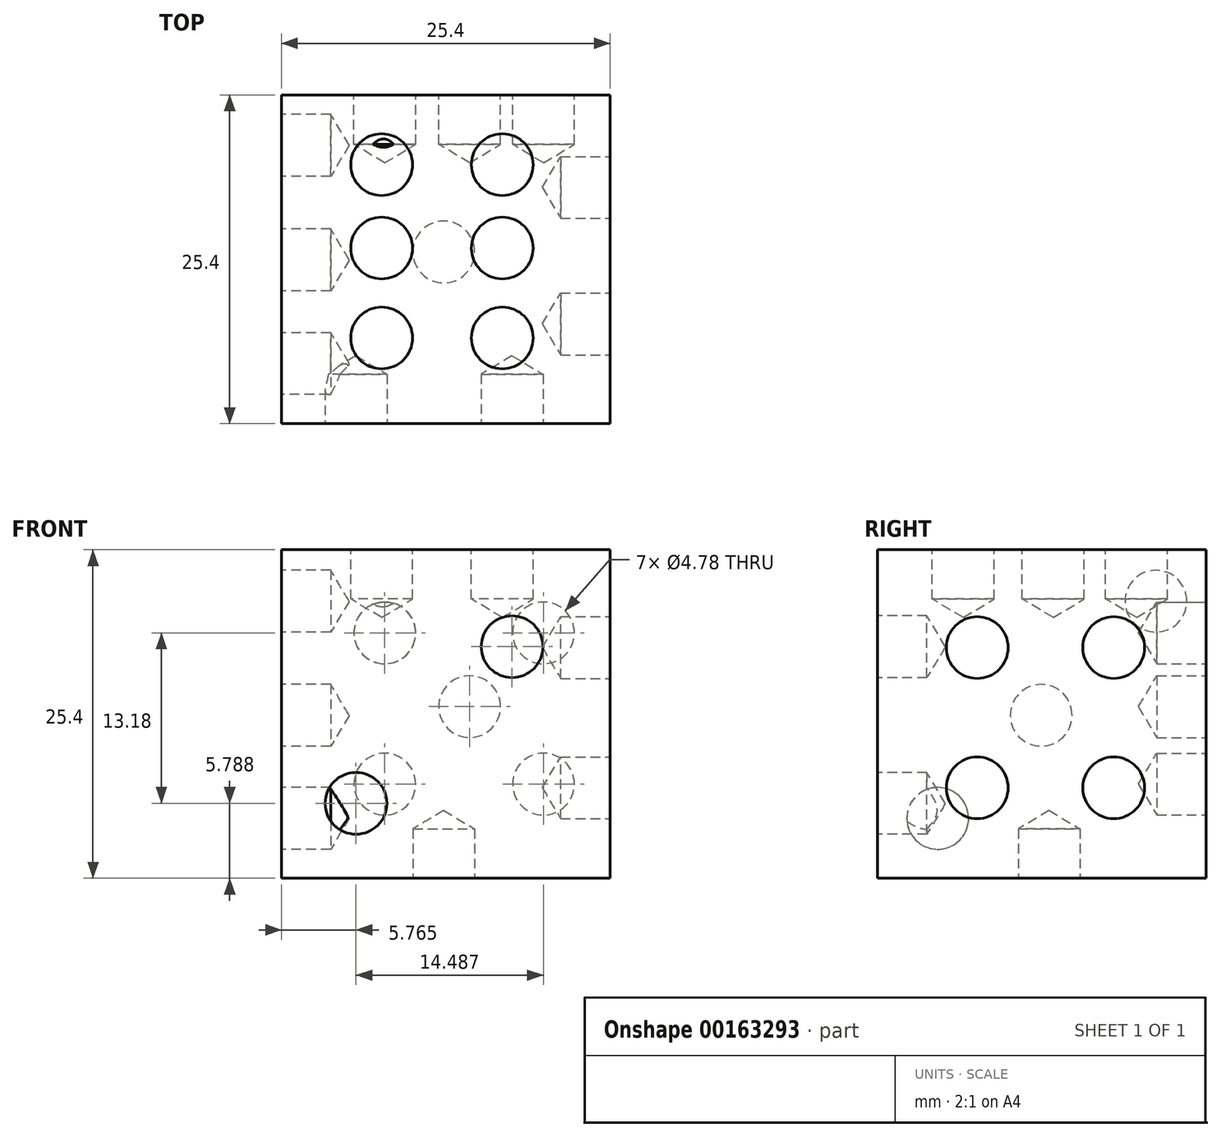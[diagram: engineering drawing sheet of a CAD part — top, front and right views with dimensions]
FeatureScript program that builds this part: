
annotation { "Feature Type Name" : "Feature", "Feature Type Description" : "" }
export const myFeature = defineFeature(function(context is Context, id is Id, definition is map)
    precondition{}
    {
        {
            var Q0;
            Q0=qCreatedBy(makeId("Top.planeOp"),FACE);
            var sketch = newSketch(context, id + "F0", { "sketchPlane" : qUnion([Q0])});
            skLineSegment(sketch, "E0.bottom", {"start": v(0, 0) * mm, "end": v(25.4, 0) * mm});
            skLineSegment(sketch, "E0.top", {"start": v(0, 25.4) * mm, "end": v(25.4, 25.4) * mm});
            skLineSegment(sketch, "E0.left", {"start": v(0, 0) * mm, "end": v(0, 25.4) * mm});
            skLineSegment(sketch, "E0.right", {"start": v(25.4, 0) * mm, "end": v(25.4, 25.4) * mm});
            skSolve(sketch);
        }
        {
            var Q0;
            Q0 = qSketchRegion(id + "F0", true);
            extrude(context, id + "F1", {"entities" : qUnion([Q0]), "depth" : 25.4 * mm});
        }
        {
            var Q0;
            Q0=qCreatedBy(makeId("Top.planeOp"),FACE);
            var sketch = newSketch(context, id + "F2", { "sketchPlane" : qUnion([Q0])});
            skPoint(sketch, "E1", {"position": v(12.55, 13.26) * mm});
            skSolve(sketch);
        }
        {
            var Q0;
            Q0=sQuery(id+"F2.wireOp",VERTEX,"E1");
            var Q1;
            Q1=makeQuery(id+"F1.opExtrude","SWEPT_BODY",BODY,{"disambiguationData":[OSD([sQuery(id+"F0.wireOp",EDGE,"E0.bottom"),sQuery(id+"F0.wireOp",EDGE,"E0.top"),sQuery(id+"F0.wireOp",EDGE,"E0.left"),sQuery(id+"F0.wireOp",EDGE,"E0.right")])]});
            hole(context, id + "F3", {"style" : HoleStyle.SIMPLE, "endStyle" : HoleEndStyle.BLIND, "oppositeDirection" : true, "holeDiameter" : 4.78 * mm, "holeDepth" : 3.8 * mm, "locations" : qUnion([Q0]), "scope" : qUnion([Q1])});
        }
        {
            var Q0;
            Q0=makeQuery(id+"F1.opExtrude","CAP_FACE",FACE,{"disambiguationData":[OSD([sQuery(id+"F0.wireOp",EDGE,"E0.bottom"),sQuery(id+"F0.wireOp",EDGE,"E0.top"),sQuery(id+"F0.wireOp",EDGE,"E0.left"),sQuery(id+"F0.wireOp",EDGE,"E0.right")])],"isStart":false});
            cPlane(context, id + "F4", {"entities" : qUnion([Q0]), "cplaneType" : CPlaneType.OFFSET, "offset" : 0 * mm, "width" : 152.4 * mm, "height" : 152.4 * mm});
        }
        {
            var Q0;
            Q0=qCreatedBy(id+"F4.planeOp",FACE);
            var sketch = newSketch(context, id + "F5", { "sketchPlane" : qUnion([Q0])});
            skPoint(sketch, "E2", {"position": v(7.74, 20.02) * mm});
            skPoint(sketch, "E3", {"position": v(17.07, 20.02) * mm});
            skPoint(sketch, "E4", {"position": v(17.07, 6.62) * mm});
            skPoint(sketch, "E5", {"position": v(7.74, 6.62) * mm});
            skPoint(sketch, "E6", {"position": v(7.74, 13.57) * mm});
            skPoint(sketch, "E7", {"position": v(17.07, 13.57) * mm});
            skSolve(sketch);
        }
        {
            var Q0;
            Q0=sQuery(id+"F5.wireOp",VERTEX,"E2");
            var Q1;
            Q1=sQuery(id+"F5.wireOp",VERTEX,"E3");
            var Q2;
            Q2=sQuery(id+"F5.wireOp",VERTEX,"E7");
            var Q3;
            Q3=sQuery(id+"F5.wireOp",VERTEX,"E6");
            var Q4;
            Q4=sQuery(id+"F5.wireOp",VERTEX,"E4");
            var Q5;
            Q5=sQuery(id+"F5.wireOp",VERTEX,"E5");
            var Q6;
            Q6=makeQuery(id+"F1.opExtrude","SWEPT_BODY",BODY,{"disambiguationData":[OSD([sQuery(id+"F0.wireOp",EDGE,"E0.bottom"),sQuery(id+"F0.wireOp",EDGE,"E0.top"),sQuery(id+"F0.wireOp",EDGE,"E0.left"),sQuery(id+"F0.wireOp",EDGE,"E0.right")])]});
            hole(context, id + "F6", {"style" : HoleStyle.SIMPLE, "endStyle" : HoleEndStyle.BLIND, "holeDiameter" : 4.78 * mm, "holeDepth" : 3.8 * mm, "locations" : qUnion([Q0, Q1, Q2, Q3, Q4, Q5]), "scope" : qUnion([Q6])});
        }
        {
            var Q0;
            Q0=makeQuery(id+"F1.opExtrude","SWEPT_FACE",FACE,{"disambiguationData":[OSD([sQuery(id+"F0.wireOp",EDGE,"E0.right")])]});
            cPlane(context, id + "F7", {"entities" : qUnion([Q0]), "cplaneType" : CPlaneType.OFFSET, "offset" : 0 * mm, "width" : 152.4 * mm, "height" : 152.4 * mm});
        }
        {
            var Q0;
            Q0=qCreatedBy(id+"F7.planeOp",FACE);
            var sketch = newSketch(context, id + "F8", { "sketchPlane" : qUnion([Q0])});
            skPoint(sketch, "E8", {"position": v(7.7, 17.83) * mm});
            skPoint(sketch, "E9", {"position": v(18.26, 17.83) * mm});
            skPoint(sketch, "E10", {"position": v(18.26, 6.99) * mm});
            skPoint(sketch, "E11", {"position": v(7.7, 6.99) * mm});
            skSolve(sketch);
        }
        {
            var Q0;
            Q0=sQuery(id+"F8.wireOp",VERTEX,"E8");
            var Q1;
            Q1=sQuery(id+"F8.wireOp",VERTEX,"E9");
            var Q2;
            Q2=sQuery(id+"F8.wireOp",VERTEX,"E10");
            var Q3;
            Q3=sQuery(id+"F8.wireOp",VERTEX,"E11");
            var Q4;
            Q4=makeQuery(id+"F1.opExtrude","SWEPT_BODY",BODY,{"disambiguationData":[OSD([sQuery(id+"F0.wireOp",EDGE,"E0.bottom"),sQuery(id+"F0.wireOp",EDGE,"E0.top"),sQuery(id+"F0.wireOp",EDGE,"E0.left"),sQuery(id+"F0.wireOp",EDGE,"E0.right")])]});
            hole(context, id + "F9", {"style" : HoleStyle.SIMPLE, "endStyle" : HoleEndStyle.BLIND, "holeDiameter" : 4.78 * mm, "holeDepth" : 3.8 * mm, "locations" : qUnion([Q0, Q1, Q2, Q3]), "scope" : qUnion([Q4])});
        }
        {
            var Q0;
            Q0=makeQuery(id+"F1.opExtrude","SWEPT_FACE",FACE,{"disambiguationData":[OSD([sQuery(id+"F0.wireOp",EDGE,"E0.left")])]});
            cPlane(context, id + "F10", {"entities" : qUnion([Q0]), "cplaneType" : CPlaneType.OFFSET, "offset" : 0 * mm, "width" : 152.4 * mm, "height" : 152.4 * mm});
        }
        {
            var Q0;
            Q0=qCreatedBy(id+"F10.planeOp",FACE);
            var sketch = newSketch(context, id + "F11", { "sketchPlane" : qUnion([Q0])});
            skPoint(sketch, "E12", {"position": v(-21.51, 21.42) * mm});
            skPoint(sketch, "E13", {"position": v(-12.65, 12.6) * mm});
            skPoint(sketch, "E14", {"position": v(-4.65, 4.63) * mm});
            skSolve(sketch);
        }
        {
            var Q0;
            Q0=sQuery(id+"F11.wireOp",VERTEX,"E12");
            var Q1;
            Q1=sQuery(id+"F11.wireOp",VERTEX,"E13");
            var Q2;
            Q2=sQuery(id+"F11.wireOp",VERTEX,"E14");
            var Q3;
            Q3=makeQuery(id+"F1.opExtrude","SWEPT_BODY",BODY,{"disambiguationData":[OSD([sQuery(id+"F0.wireOp",EDGE,"E0.bottom"),sQuery(id+"F0.wireOp",EDGE,"E0.top"),sQuery(id+"F0.wireOp",EDGE,"E0.left"),sQuery(id+"F0.wireOp",EDGE,"E0.right")])]});
            hole(context, id + "F12", {"style" : HoleStyle.SIMPLE, "endStyle" : HoleEndStyle.BLIND, "holeDiameter" : 4.78 * mm, "holeDepth" : 3.8 * mm, "locations" : qUnion([Q0, Q1, Q2]), "scope" : qUnion([Q3])});
        }
        {
            var Q0;
            Q0=makeQuery(id+"F1.opExtrude","SWEPT_FACE",FACE,{"disambiguationData":[OSD([sQuery(id+"F0.wireOp",EDGE,"E0.bottom")])]});
            cPlane(context, id + "F13", {"entities" : qUnion([Q0]), "cplaneType" : CPlaneType.OFFSET, "offset" : 0 * mm, "width" : 152.4 * mm, "height" : 152.4 * mm});
        }
        {
            var Q0;
            Q0=qCreatedBy(id+"F13.planeOp",FACE);
            var sketch = newSketch(context, id + "F14", { "sketchPlane" : qUnion([Q0])});
            skPoint(sketch, "E15", {"position": v(5.77, 5.79) * mm});
            skPoint(sketch, "E16", {"position": v(17.83, 17.9) * mm});
            skSolve(sketch);
        }
        {
            var Q0;
            Q0=sQuery(id+"F14.wireOp",VERTEX,"E15");
            var Q1;
            Q1=sQuery(id+"F14.wireOp",VERTEX,"E16");
            var Q2;
            Q2=makeQuery(id+"F1.opExtrude","SWEPT_BODY",BODY,{"disambiguationData":[OSD([sQuery(id+"F0.wireOp",EDGE,"E0.bottom"),sQuery(id+"F0.wireOp",EDGE,"E0.top"),sQuery(id+"F0.wireOp",EDGE,"E0.left"),sQuery(id+"F0.wireOp",EDGE,"E0.right")])]});
            hole(context, id + "F15", {"style" : HoleStyle.SIMPLE, "endStyle" : HoleEndStyle.BLIND, "holeDiameter" : 4.78 * mm, "holeDepth" : 3.8 * mm, "locations" : qUnion([Q0, Q1]), "scope" : qUnion([Q2])});
        }
        {
            var Q0;
            Q0=makeQuery(id+"F1.opExtrude","SWEPT_FACE",FACE,{"disambiguationData":[OSD([sQuery(id+"F0.wireOp",EDGE,"E0.top")])]});
            cPlane(context, id + "F16", {"entities" : qUnion([Q0]), "cplaneType" : CPlaneType.OFFSET, "offset" : 0 * mm, "width" : 152.4 * mm, "height" : 152.4 * mm});
        }
        {
            var Q0;
            Q0=qCreatedBy(id+"F16.planeOp",FACE);
            var sketch = newSketch(context, id + "F17", { "sketchPlane" : qUnion([Q0])});
            skPoint(sketch, "E17", {"position": v(-20.25, 18.97) * mm});
            skPoint(sketch, "E18", {"position": v(-7.99, 18.97) * mm});
            skPoint(sketch, "E19", {"position": v(-7.99, 7.27) * mm});
            skPoint(sketch, "E20", {"position": v(-20.25, 7.27) * mm});
            skPoint(sketch, "E21", {"position": v(-14.55, 13.26) * mm});
            skSolve(sketch);
        }
        {
            var Q0;
            Q0=sQuery(id+"F17.wireOp",VERTEX,"E17");
            var Q1;
            Q1=sQuery(id+"F17.wireOp",VERTEX,"E18");
            var Q2;
            Q2=sQuery(id+"F17.wireOp",VERTEX,"E21");
            var Q3;
            Q3=sQuery(id+"F17.wireOp",VERTEX,"E20");
            var Q4;
            Q4=sQuery(id+"F17.wireOp",VERTEX,"E19");
            var Q5;
            Q5=makeQuery(id+"F1.opExtrude","SWEPT_BODY",BODY,{"disambiguationData":[OSD([sQuery(id+"F0.wireOp",EDGE,"E0.bottom"),sQuery(id+"F0.wireOp",EDGE,"E0.top"),sQuery(id+"F0.wireOp",EDGE,"E0.left"),sQuery(id+"F0.wireOp",EDGE,"E0.right")])]});
            hole(context, id + "F18", {"style" : HoleStyle.SIMPLE, "endStyle" : HoleEndStyle.BLIND, "holeDiameter" : 4.78 * mm, "holeDepth" : 3.8 * mm, "locations" : qUnion([Q0, Q1, Q2, Q3, Q4]), "scope" : qUnion([Q5])});
        }
    });
